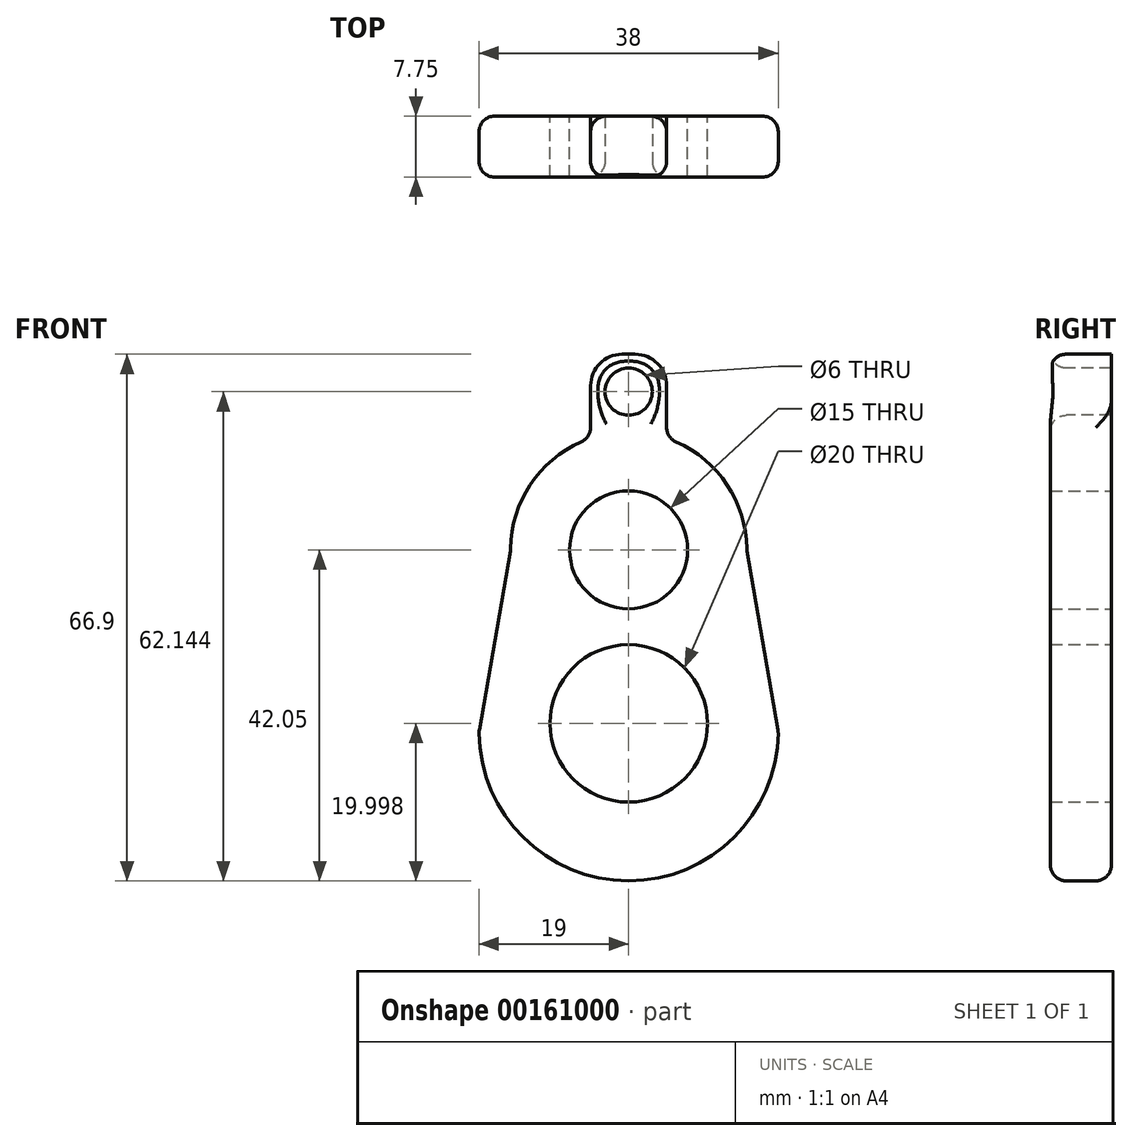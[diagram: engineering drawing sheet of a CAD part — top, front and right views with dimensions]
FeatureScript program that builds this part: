
annotation { "Feature Type Name" : "Feature", "Feature Type Description" : "" }
export const myFeature = defineFeature(function(context is Context, id is Id, definition is map)
    precondition{}
    {
        {
            var Q0;
            Q0=qCreatedBy(makeId("Front.planeOp"),FACE);
            var sketch = newSketch(context, id + "F0", { "sketchPlane" : qUnion([Q0])});
            skCircle(sketch, "E0", {"center": v(0, -23.05) * mm, "radius": 19 * mm});
            skCircle(sketch, "E1", {"center": v(0, -0.03) * mm, "radius": 15 * mm});
            skPoint(sketch, "E2", {"position": v(-0.83, 14.95) * mm});
            skPoint(sketch, "E3", {"position": v(0, -42.05) * mm});
            skLineSegment(sketch, "E4", {"start": v(-4.83, 14.17) * mm, "end": v(-4.83, 20.85) * mm});
            skLineSegment(sketch, "E5", {"start": v(-0.83, 24.85) * mm, "end": v(0, 24.85) * mm});
            skLineSegment(sketch, "E6", {"start": v(0, 24.85) * mm, "end": v(0.83, 24.85) * mm});
            skLineSegment(sketch, "E7", {"start": v(4.83, 20.85) * mm, "end": v(4.83, 14.17) * mm});
            skPoint(sketch, "E8.visualSharp", {"position": v(-4.83, 24.85) * mm});
            skArc(sketch, "E8.filletArc", {"start": v(-0.83, 24.85) * mm, "mid": v(-3.66, 23.68) * mm, "end": v(-4.83, 20.85) * mm});
            skPoint(sketch, "E9.visualSharp", {"position": v(4.83, 24.85) * mm});
            skArc(sketch, "E9.filletArc", {"start": v(4.83, 20.85) * mm, "mid": v(3.66, 23.68) * mm, "end": v(0.83, 24.85) * mm});
            skLineSegment(sketch, "E10", {"start": v(-15, 0) * mm, "end": v(-19, -23.05) * mm});
            skLineSegment(sketch, "E11", {"start": v(15, 0) * mm, "end": v(19, -23.05) * mm});
            skSolve(sketch);
        }
        {
            var Q0;
            {var subQ0=sQuery(id+"F0.wireOp",EDGE,"E1");var subQ5=sQuery(id+"F0.wireOp",EDGE,"E0");var subQ6=makeQuery(id+"F0.imprint","INTERSECT",VERTEX,{"disambiguationData":[OD(0.0)],"derivedFrom":[subQ5,subQ0]});Q0=makeQuery(id+"F0.imprint","IMPRINT",FACE,{"disambiguationData":[TD([[makeQuery(id+"F0.imprint","IMPRINT",EDGE,{"disambiguationData":[TD([[subQ6,-1.0]])],"derivedFrom":subQ5}),-1.0]])]});}
            var Q1;
            {var subQ0=sQuery(id+"F0.wireOp",EDGE,"E1");var subQ1=sQuery(id+"F0.wireOp",EDGE,"E0");var subQ2=makeQuery(id+"F0.imprint","INTERSECT",VERTEX,{"disambiguationData":[OD(0.0)],"derivedFrom":[subQ1,subQ0]});Q1=makeQuery(id+"F0.imprint","IMPRINT",FACE,{"disambiguationData":[TD([[makeQuery(id+"F0.imprint","IMPRINT",EDGE,{"disambiguationData":[TD([[subQ2,-1.0]])],"derivedFrom":subQ1}),1.0]])]});}
            var Q2;
            {var subQ1=sQuery(id+"F0.wireOp",EDGE,"E0");var subQ7=sQuery(id+"F0.wireOp",EDGE,"E11");var subQ9=makeQuery(id+"F0.imprint","INTERSECT",VERTEX,{"disambiguationData":[OD(1.0)],"derivedFrom":[subQ1,subQ7]});Q2=makeQuery(id+"F0.imprint","IMPRINT",FACE,{"disambiguationData":[TD([[makeQuery(id+"F0.imprint","IMPRINT",EDGE,{"disambiguationData":[TD([[subQ9,-1.0]])],"derivedFrom":subQ1}),1.0]])]});}
            var Q3;
            {var subQ0=sQuery(id+"F0.wireOp",EDGE,"E11");var subQ1=sQuery(id+"F0.wireOp",EDGE,"E0");var subQ2=makeQuery(id+"F0.imprint","INTERSECT",VERTEX,{"disambiguationData":[OD(1.0)],"derivedFrom":[subQ1,subQ0]});Q3=makeQuery(id+"F0.imprint","IMPRINT",FACE,{"disambiguationData":[TD([[makeQuery(id+"F0.imprint","IMPRINT",EDGE,{"disambiguationData":[TD([[subQ2,-1.0]])],"derivedFrom":subQ1}),-1.0]])]});}
            var Q4;
            {var subQ0=sQuery(id+"F0.wireOp",EDGE,"E10");var subQ1=sQuery(id+"F0.wireOp",EDGE,"E0");var subQ2=makeQuery(id+"F0.imprint","INTERSECT",VERTEX,{"disambiguationData":[OD(1.0)],"derivedFrom":[subQ1,subQ0]});Q4=makeQuery(id+"F0.imprint","IMPRINT",FACE,{"disambiguationData":[TD([[makeQuery(id+"F0.imprint","IMPRINT",EDGE,{"disambiguationData":[TD([[subQ2,1.0]])],"derivedFrom":subQ1}),-1.0]])]});}
            var Q5;
            {var subQ0=sQuery(id+"F0.wireOp",EDGE,"E4");Q5=makeQuery(id+"F0.imprint","IMPRINT",FACE,{"disambiguationData":[TD([[makeQuery(id+"F0.imprint","IMPRINT",EDGE,{"derivedFrom":subQ0}),-1.0]])]});}
            extrude(context, id + "F1", {"entities" : qUnion([Q0, Q1, Q2, Q3, Q4, Q5]), "depth" : 7.75 * mm});
        }
        {
            var Q0;
            Q0=makeQuery(id+"F1.opExtrude","CAP_FACE",FACE,{"disambiguationData":[OSD([sQuery(id+"F0.wireOp",EDGE,"E0"),sQuery(id+"F0.wireOp",EDGE,"E1"),sQuery(id+"F0.wireOp",EDGE,"E4"),sQuery(id+"F0.wireOp",EDGE,"E5"),sQuery(id+"F0.wireOp",EDGE,"E6"),sQuery(id+"F0.wireOp",EDGE,"E7"),sQuery(id+"F0.wireOp",EDGE,"E8.filletArc"),sQuery(id+"F0.wireOp",EDGE,"E9.filletArc"),sQuery(id+"F0.wireOp",EDGE,"E10"),sQuery(id+"F0.wireOp",EDGE,"E11")])],"isStart":false});
            var sketch = newSketch(context, id + "F2", { "sketchPlane" : qUnion([Q0])});
            skCircle(sketch, "E12", {"center": v(0, 20.1) * mm, "radius": 3.33 * mm});
            skSolve(sketch);
        }
        {
            var Q0;
            Q0=sQuery(id+"F2.wireOp",VERTEX,"E12.center");
            var Q1;
            Q1=makeQuery(id+"F1.opExtrude","SWEPT_BODY",BODY,{"disambiguationData":[OSD([sQuery(id+"F0.wireOp",EDGE,"E0"),sQuery(id+"F0.wireOp",EDGE,"E1"),sQuery(id+"F0.wireOp",EDGE,"E4"),sQuery(id+"F0.wireOp",EDGE,"E5"),sQuery(id+"F0.wireOp",EDGE,"E6"),sQuery(id+"F0.wireOp",EDGE,"E7"),sQuery(id+"F0.wireOp",EDGE,"E8.filletArc"),sQuery(id+"F0.wireOp",EDGE,"E9.filletArc"),sQuery(id+"F0.wireOp",EDGE,"E10"),sQuery(id+"F0.wireOp",EDGE,"E11")])]});
            hole(context, id + "F3", {"style" : HoleStyle.SIMPLE, "endStyle" : HoleEndStyle.THROUGH, "holeDiameter" : 6 * mm, "locations" : qUnion([Q0]), "scope" : qUnion([Q1]), "isTappedThrough" : true});
        }
        {
            var Q0;
            Q0=makeQuery(id+"F1.opExtrude","CAP_FACE",FACE,{"disambiguationData":[OSD([sQuery(id+"F0.wireOp",EDGE,"E0"),sQuery(id+"F0.wireOp",EDGE,"E1"),sQuery(id+"F0.wireOp",EDGE,"E4"),sQuery(id+"F0.wireOp",EDGE,"E5"),sQuery(id+"F0.wireOp",EDGE,"E6"),sQuery(id+"F0.wireOp",EDGE,"E7"),sQuery(id+"F0.wireOp",EDGE,"E8.filletArc"),sQuery(id+"F0.wireOp",EDGE,"E9.filletArc"),sQuery(id+"F0.wireOp",EDGE,"E10"),sQuery(id+"F0.wireOp",EDGE,"E11")])],"isStart":false});
            var Q1;
            {var subQ0=sQuery(id+"F0.wireOp",EDGE,"E1");Q1=makeQuery(id+"F1.opExtrude","CAP_EDGE",EDGE,{"disambiguationData":[OSD([subQ0]),TDD([makeQuery(id+"F0.imprint","IMPRINT",EDGE,{"disambiguationData":[TD([[makeQuery(id+"F0.imprint","INTERSECT",VERTEX,{"derivedFrom":[subQ0,sQuery(id+"F0.wireOp",EDGE,"E4")]}),-1.0]])],"derivedFrom":subQ0})])],"isStart":false});}
            var Q2;
            {var subQ0=sQuery(id+"F0.wireOp",EDGE,"E1");Q2=makeQuery(id+"F1.opExtrude","SWEPT_FACE",FACE,{"disambiguationData":[OSD([subQ0]),TDD([makeQuery(id+"F0.imprint","IMPRINT",EDGE,{"disambiguationData":[TD([[makeQuery(id+"F0.imprint","INTERSECT",VERTEX,{"derivedFrom":[subQ0,sQuery(id+"F0.wireOp",EDGE,"E4")]}),-1.0]])],"derivedFrom":subQ0})])]});}
            var Q3;
            Q3=makeQuery(id+"F1.opExtrude","SWEPT_FACE",FACE,{"disambiguationData":[OSD([sQuery(id+"F0.wireOp",EDGE,"E10")])]});
            var Q4;
            Q4=makeQuery(id+"F1.opExtrude","SWEPT_FACE",FACE,{"disambiguationData":[OSD([sQuery(id+"F0.wireOp",EDGE,"E0")])]});
            var Q5;
            Q5=makeQuery(id+"F1.opExtrude","SWEPT_FACE",FACE,{"disambiguationData":[OSD([sQuery(id+"F0.wireOp",EDGE,"E11")])]});
            var Q6;
            {var subQ0=sQuery(id+"F0.wireOp",EDGE,"E1");Q6=makeQuery(id+"F1.opExtrude","SWEPT_FACE",FACE,{"disambiguationData":[OSD([subQ0]),TDD([makeQuery(id+"F0.imprint","IMPRINT",EDGE,{"disambiguationData":[TD([[makeQuery(id+"F0.imprint","INTERSECT",VERTEX,{"derivedFrom":[subQ0,sQuery(id+"F0.wireOp",EDGE,"E7")]}),1.0]])],"derivedFrom":subQ0})])]});}
            var Q7;
            Q7=makeQuery(id+"F3.hole-0.boolean.opBoolean","COPY",FACE,{"derivedFrom":makeQuery(id+"F3.hole-0.opRevolve","SWEPT_FACE",FACE,{"disambiguationData":[OSD([sQuery(id+"F3.hole-0.sketch.wireOp",EDGE,"core_line_2")])]})});
            fillet(context, id + "F4", {"entities" : qUnion([Q0, Q1, Q2, Q3, Q4, Q5, Q6, Q7]), "radius" : 2 * mm, "tangentPropagation" : true, "allowEdgeOverflow" : false});
        }
        {
            var Q0;
            Q0=makeQuery(id+"F1.opExtrude","CAP_FACE",FACE,{"disambiguationData":[OSD([sQuery(id+"F0.wireOp",EDGE,"E0"),sQuery(id+"F0.wireOp",EDGE,"E1"),sQuery(id+"F0.wireOp",EDGE,"E4"),sQuery(id+"F0.wireOp",EDGE,"E5"),sQuery(id+"F0.wireOp",EDGE,"E6"),sQuery(id+"F0.wireOp",EDGE,"E7"),sQuery(id+"F0.wireOp",EDGE,"E8.filletArc"),sQuery(id+"F0.wireOp",EDGE,"E9.filletArc"),sQuery(id+"F0.wireOp",EDGE,"E10"),sQuery(id+"F0.wireOp",EDGE,"E11")])],"isStart":true});
            var sketch = newSketch(context, id + "F5", { "sketchPlane" : qUnion([Q0])});
            skCircle(sketch, "E13", {"center": v(0, 0) * mm, "radius": 7.5 * mm});
            skCircle(sketch, "E14", {"center": v(0, -22.05) * mm, "radius": 10 * mm});
            skSolve(sketch);
        }
        {
            var Q0;
            Q0=sQuery(id+"F5.wireOp",VERTEX,"E13.center");
            var Q1;
            Q1=makeQuery(id+"F1.opExtrude","SWEPT_BODY",BODY,{"disambiguationData":[OSD([sQuery(id+"F0.wireOp",EDGE,"E0"),sQuery(id+"F0.wireOp",EDGE,"E1"),sQuery(id+"F0.wireOp",EDGE,"E4"),sQuery(id+"F0.wireOp",EDGE,"E5"),sQuery(id+"F0.wireOp",EDGE,"E6"),sQuery(id+"F0.wireOp",EDGE,"E7"),sQuery(id+"F0.wireOp",EDGE,"E8.filletArc"),sQuery(id+"F0.wireOp",EDGE,"E9.filletArc"),sQuery(id+"F0.wireOp",EDGE,"E10"),sQuery(id+"F0.wireOp",EDGE,"E11")])]});
            hole(context, id + "F6", {"style" : HoleStyle.SIMPLE, "endStyle" : HoleEndStyle.THROUGH, "holeDiameter" : 15 * mm, "locations" : qUnion([Q0]), "scope" : qUnion([Q1]), "isTappedThrough" : true});
        }
        {
            var Q0;
            Q0=sQuery(id+"F5.wireOp",VERTEX,"E14.center");
            var Q1;
            Q1=makeQuery(id+"F1.opExtrude","SWEPT_BODY",BODY,{"disambiguationData":[OSD([sQuery(id+"F0.wireOp",EDGE,"E0"),sQuery(id+"F0.wireOp",EDGE,"E1"),sQuery(id+"F0.wireOp",EDGE,"E4"),sQuery(id+"F0.wireOp",EDGE,"E5"),sQuery(id+"F0.wireOp",EDGE,"E6"),sQuery(id+"F0.wireOp",EDGE,"E7"),sQuery(id+"F0.wireOp",EDGE,"E8.filletArc"),sQuery(id+"F0.wireOp",EDGE,"E9.filletArc"),sQuery(id+"F0.wireOp",EDGE,"E10"),sQuery(id+"F0.wireOp",EDGE,"E11")])]});
            hole(context, id + "F7", {"style" : HoleStyle.SIMPLE, "endStyle" : HoleEndStyle.THROUGH, "holeDiameter" : 20 * mm, "locations" : qUnion([Q0]), "scope" : qUnion([Q1]), "isTappedThrough" : true});
        }
    });
